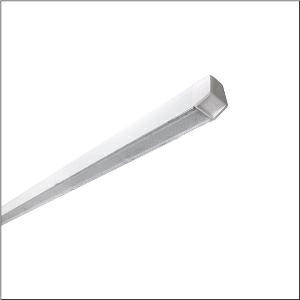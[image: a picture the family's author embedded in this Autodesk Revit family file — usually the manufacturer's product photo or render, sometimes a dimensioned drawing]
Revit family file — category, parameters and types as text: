
# Revit family: licross_r__21_recessed_ho_52ul1edv4d5f00s_4953
name_source: partatom
category: Lighting Fixtures
units: mm (PartAtom-declared; Revit-internal decimal feet)

## family parameters
Cut with Voids When Loaded = No
Host = Face
Light Source = No
Part Type = Normal
Room Calculation Point = No
Round Connector Dimension = Use Diameter
Shared = No

## types (1)
- --- (1 x LED, 13820 lm, 87.2 W, 4000K)
    Apparent Load = 87 VA
    CIE Flux Codes = 85 95 99 100 100
    Color Rendering = 80
    Color Temperature = 4000K
    Default Elevation = 1800 mm
    Description = Licross® 21 Recessed HO, single luminaire, primary optical cover: cover, of PMMA, light emission: direct distribution, primary light characteristic: symmetric, installation type: slip-in mounting, LED, rated luminous flux: 13.820lm, luminous efficacy: 159lm/W, light colour: 840, colour temperature: 4000K, control gear: ECG DALI, with terminal, 5-pole, max. 2.5mm², mains connection: 230V, AC, 50/60Hz, rated input power: 87W, Licross® LED insert, of sheet steel, galvanised, coil coated, white, with terminals, length: 2.327mm, width: 70mm, height: 71mm, end cap, of PC, white, mounting rail, of sheet steel, galvanised, white, protection rating (complete): IP20, insulation class (complete): insulation class I (protective earthing), certification: CE, ENEC, VDE, UKCA, impact resistance: IK06, permissible operating ambient temperature: -25..+35°C, corresponds to IFS (International Featured Standards) requirements for safety and quality in the food industry, reducing of maximum allowable ambient temperature of 5°C with ceiling mounting, LABS conformity tested according to VDMA 24364:2018-05, packaging unit: 1 piece
    Height = 58 mm
    Lamp = 1 x LED
    Lamp Light Flux = 13820 lm
    Lamp Power = 87.2 W
    Lamp count = 1
    Length = 2250 mm
    Luminous efficacy = 158 lm/W
    Manufacturer = Siteco
    ModVariant = No
    Model = 52UL1EDV4D5F00S
    Mounting Place = Ceiling
    Mounting Type = Pendant
    Number of Poles = 1
    OnlyDefault = Yes
    Power Factor = 1
    Product Name = Licross® 21 Recessed HO
    Product group = single luminaire
    ProductGroupID = 907
    Protection Class = Protection class I
    Protection Degree = IP 20
    RLX_Detail_Level = 1
    RLX_Emergency_Light_Flux = 0 lm
    RLX_Emergency_Type = 0
    RLX_Emergency_Type_DB = No
    RlxData = <blob elided: 32093 chars, md5=1169cdc4>
    Socket = socket
    Standby Power = 0 W
    System Light Flux = 13820 lm
    System Power = 87 W
    Type Comments = factory setting: luminous flux: 100 % | dim-lin: 254 | 405 mA
    Type Image = l_1006979.jpg
    URL = http://relux.com
    VarID = @adj_130805
    Voltage = 0 V
    Weight = 0.00 kg
    Width = 66 mm

## geometry (parser evidence)
native form markers: Blend x4, Sweep x11
no freeform markers — native parametric forms only
